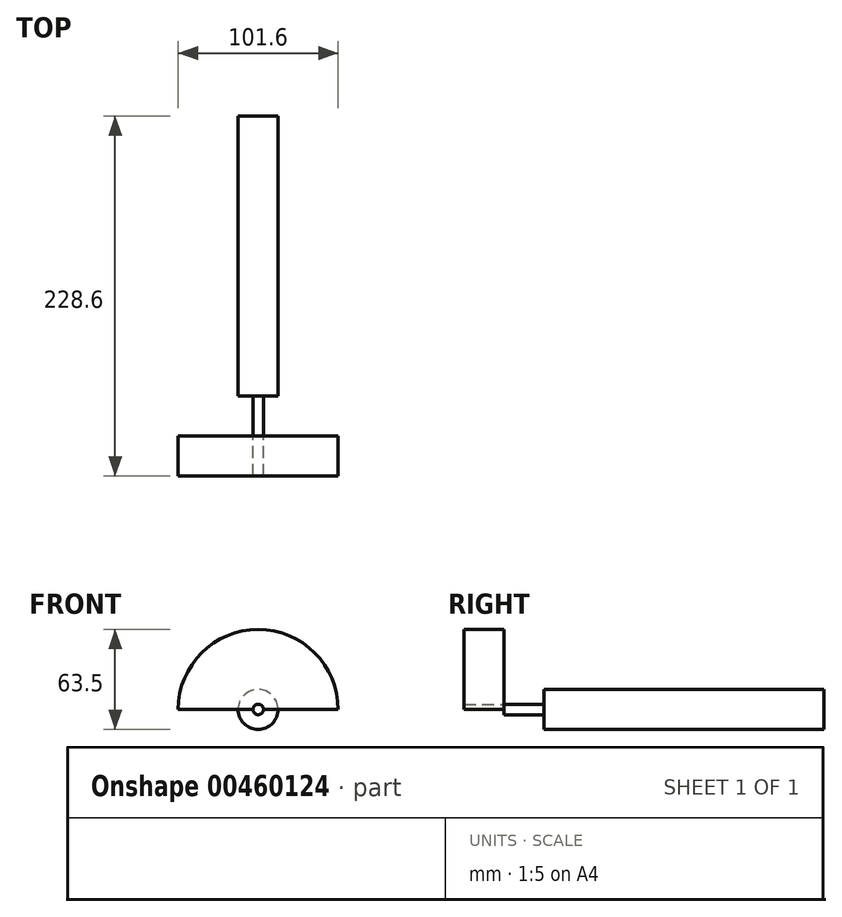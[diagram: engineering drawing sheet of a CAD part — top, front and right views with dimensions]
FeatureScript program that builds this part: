
annotation { "Feature Type Name" : "Feature", "Feature Type Description" : "" }
export const myFeature = defineFeature(function(context is Context, id is Id, definition is map)
    precondition{}
    {
        {
            var Q0;
            Q0=qCreatedBy(makeId("Front.planeOp"),FACE);
            var sketch = newSketch(context, id + "F0", { "sketchPlane" : qUnion([Q0])});
            skCircle(sketch, "E0", {"center": v(0, 0) * mm, "radius": 12.7 * mm});
            skSolve(sketch);
        }
        {
            var Q0;
            Q0=makeQuery(id+"F0.imprint","IMPRINT",FACE,{"disambiguationData":[TD([[makeQuery(id+"F0.imprint","IMPRINT",EDGE,{"derivedFrom":sQuery(id+"F0.wireOp",EDGE,"E0")}),1.0]])]});
            extrude(context, id + "F1", {"entities" : qUnion([Q0]), "depth" : 177.8 * mm});
        }
        {
            var Q0;
            Q0=makeQuery(id+"F1.opExtrude","CAP_FACE",FACE,{"disambiguationData":[OSD([sQuery(id+"F0.wireOp",EDGE,"E0")])],"isStart":false});
            var sketch = newSketch(context, id + "F2", { "sketchPlane" : qUnion([Q0])});
            skCircle(sketch, "E1", {"center": v(0, 0) * mm, "radius": 3.34 * mm});
            skSolve(sketch);
        }
        {
            var Q0;
            Q0=makeQuery(id+"F2.imprint","IMPRINT",FACE,{"disambiguationData":[TD([[makeQuery(id+"F2.imprint","IMPRINT",EDGE,{"derivedFrom":sQuery(id+"F2.wireOp",EDGE,"E1")}),1.0]])]});
            extrude(context, id + "F3", {"entities" : qUnion([Q0]), "operationType" : NewBodyOperationType.ADD, "depth" : 25.4 * mm});
        }
        {
            var Q0;
            Q0=makeQuery(id+"F3.opExtrude","CAP_FACE",FACE,{"disambiguationData":[OSD([sQuery(id+"F2.wireOp",EDGE,"E1")])],"isStart":false});
            var sketch = newSketch(context, id + "F4", { "sketchPlane" : qUnion([Q0])});
            skArc(sketch, "E2", {"start": v(50.8, 0) * mm, "mid": v(0, 50.8) * mm, "end": v(-50.8, 0) * mm});
            skLineSegment(sketch, "E3", {"start": v(-50.8, 0) * mm, "end": v(50.8, 0) * mm});
            skSolve(sketch);
        }
        {
            var Q0;
            {var subQ0=sQuery(id+"F4.wireOp",EDGE,"E2");Q0=makeQuery(id+"F4.imprint","IMPRINT",FACE,{"disambiguationData":[TD([[makeQuery(id+"F4.imprint","IMPRINT",EDGE,{"derivedFrom":subQ0}),1.0]])]});}
            extrude(context, id + "F5", {"entities" : qUnion([Q0]), "depth" : 25.4 * mm});
        }
    });
